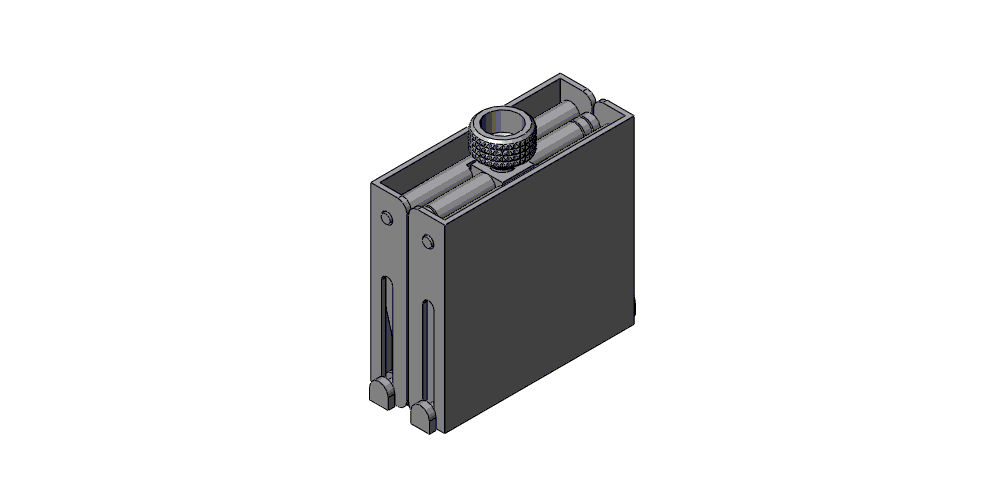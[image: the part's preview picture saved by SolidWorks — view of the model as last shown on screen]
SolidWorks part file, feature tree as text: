
SOLIDWORKS PART (.sldprt)
format: sldprt  version: not decoded by parser v0  size: 1,744,896 bytes
history: native  units: mm
features: sketch x38, extrude x17, mirror x9, cut_extrude x8, plane x5, revolve x4, boolean_combine x4, chamfer x3, pattern_linear x2, helix x2, sweep x2, cut_revolve x2, material x1, fillet x1, pattern_circular x1 (+13 scaffold rows collapsed)
feature tree (112):
  scaffold x13  (default folders/planes/origin — collapsed)
  material  "Material <not specified>"
  sketch  "Sketch1"  dims[c1.D1=80.0mm c1.D2=14.0mm c2.D1=80.0mm c2.D5=2.0mm c2.D6=1.0mm c2.D7=5.0mm]
  sketch  "Sketch2"  dims[c1.D2=2.5mm c1.D5=4.0mm c1.D6=5.0mm c1.D1=35.0mm c1.D3=35.0mm c1.D4=10.0mm c2.D1=65.0mm c2.D3=40.0mm c2.D5=60.0mm c3.D5=20.0deg c4.D5=60.0mm c5.D5=20.0deg c6.D5=60.0mm c7.D5=~8.063246deg c8.D5=80.0mm c9.D5=8.5deg c10.D5=5.25mm]
  cut_extrude  "Cut-Extrude1"  Depth=10mm
  fillet  "Fillet1"  Radius=4mm
  sketch  "Sketch3"  dims[c1.D1=3.5mm c1.D4=5.0mm c1.D2=60.0mm c2.D2=8.0deg c2.D3=~65.638792mm c2.D1=8.25mm c2.D4=1.0mm]
  extrude  "Boss-Extrude1"  Depth=3mm
  sketch  "Sketch4"  dims[c1.D1=60.0mm c2.D1=10.0deg c3.D1=~9.135154mm]
  extrude  "Boss-Extrude3"  Depth=3mm
  pattern_linear  "LPattern1"  Count1=2 Count2=1 Spacing1=9.135154mm Spacing2=10mm
  sketch  "Sketch5"
  plane  "Plane1"
  plane  "Plane2"
  plane  "Plane3"
  mirror  "Mirror1"
  mirror  "Mirror2"
  sketch  "Sketch9"
  extrude  "Boss-Extrude5"  Depth=0.65mm
  sketch  "Sketch10"  dims[D1=0.5mm]
  extrude  "Boss-Extrude6"  Depth=0.65mm
  sketch  "Sketch12"
  cut_extrude  "Cut-Extrude2"  Depth=0.2mm
  sketch  "Sketch13"  dims[D1=5.0mm]
  extrude  "Boss-Extrude8"  Depth=0.65mm
  sketch  "Sketch14"
  extrude  "Boss-Extrude9"  [1 undecoded]
  sketch  "Sketch30"
  cut_extrude  "Cut-Extrude8"  Depth=3mm
  sketch  "Sketch31"
  extrude  "Boss-Extrude18"  Depth=4.15mm
  mirror  "Mirror20"
  sketch  "Sketch23"  dims[c1.D1=1.0mm c1.D2=1.0mm c1.D3=~4.986778mm c2.D3=82.0deg c3.D3=~9.135154mm c4.D3=82.0deg c5.D3=5.125mm c6.D3=82.0deg c6.D4=~4.580357mm c7.D4=82.0deg]
  extrude  "Boss-Extrude12"  Depth=9mm
  pattern_linear  "LPattern2"  Count1=2 Count2=2 Spacing1=34.85mm Spacing2=34.85mm
  sketch  "Sketch26"
  extrude  "Boss-Extrude15"  [1 undecoded]
  sketch  "Sketch28"  dims[c1.D1=~9.135154mm c2.D1=172.0deg c3.D1=~65.638792mm c4.D1=172.0deg c5.D1=8.25mm c6.D1=82.0deg c6.D2=8.25mm c7.D2=82.0deg c8.D2=~9.135154mm c9.D2=82.0deg]
  extrude  "Boss-Extrude16"  Depth=3mm
  mirror  "Mirror14"
  sketch  "Sketch33"  dims[D1=9.0mm]
  cut_extrude  "Cut-Extrude9"  [1 undecoded]
  sketch  "Sketch35"  dims[D1=14.0mm]
  extrude  "Boss-Extrude19"  Depth=9.2mm
  sketch  "Sketch36"  dims[D1=10.0mm]
  extrude  "Boss-Extrude20"  Depth=10mm
  sketch  "Sketch65"  dims[D1=0.8mm]
  cut_extrude  "Cut-Extrude16"  Depth=2mm
  sketch  "Sketch37"  dims[c1.D1=1.0mm c1.D2=~6.385154mm c2.D1=~6.385154mm c2.D2=1.0mm c3.D1=~6.385154mm]
  cut_extrude  "Cut-Extrude10"  [1 undecoded]
  sketch  "Sketch40"  dims[c1.D1=0.8mm c1.D2=~5.985529mm c2.D2=50.0deg c2.D3=10.0mm c2.D4=0.4mm c2.D5=3.0mm c2.D6=3.0mm]
  revolve  "Revolve1"  Angle=360deg
  chamfer  "Chamfer3"  Distance=1mm Angle=45deg
  sketch  "Sketch44"
  helix  "Helix/Spiral2"  Pitch=11.25mm
  sketch  "Sketch45"  dims[D1=2.0mm D2=1.25mm]
  sweep  "Cut-Sweep1"
  plane  "Plane4"  Offset=2mm
  sketch  "Sketch47"  dims[D1=0.0mm]
  helix  "Helix/Spiral3"  Pitch=49.5mm
  sketch  "Sketch46"  dims[D1=1.25mm D2=2.0mm D3=~2.000016mm]
  sweep  "Sweep3"
  sketch  "Sketch49"
  cut_extrude  "Cut-Extrude11"  Depth=8mm
  sketch  "Sketch52"  dims[D1=0.0mm]
  extrude  "Boss-Extrude23"  Depth=10mm
  sketch  "Sketch59"  dims[c1.D1=2.0mm c1.D2=3.5mm c1.D3=3.5mm c2.D3=8.0deg]
  extrude  "Boss-Extrude24"  Depth=3.5mm
  chamfer  "Chamfer4"  Distance=3.5mm Angle=45deg
  mirror  "Mirror21"
  sketch  "Sketch60"  dims[c1.D1=8.25mm c1.D2=~10.470798mm c2.D1=0.5mm c2.D2=4.0mm]
  extrude  "Boss-Extrude25"  Depth=2mm
  mirror  "Mirror22"
  chamfer  "Chamfer5"  Distance=2mm Angle=60deg
  sketch  "Sketch62"  dims[D1=0.5mm]
  revolve  "Revolve2"  Angle=360deg
  sketch  "Sketch63"  dims[D1=2.1mm]
  cut_extrude  "Cut-Extrude15"  [1 undecoded]
  pattern_circular  "CirPattern1"  Count=32 Angle=11.25deg
  sketch  "Sketch69"
  plane  "Plane5"
  sketch  "Sketch71"  dims[c1.D1=7.5mm c1.D2=~2.179387mm c2.D2=45.0deg c2.D1=0.75mm c3.D2=2.5mm]
  cut_revolve  "Cut-Revolve1"  Angle=360deg
  sketch  "Sketch74"
  cut_revolve  "Cut-Revolve2"  Angle=360deg
  mirror  "Mirror23"
  sketch  "Sketch72"  dims[c1.D1=~1.228622mm c2.D1=45.0deg c3.D1=1.125mm c4.D1=45.0deg]
  revolve  "Revolve3"  Angle=360deg
  sketch  "Sketch75"
  revolve  "Revolve4"  Angle=360deg
  mirror  "Mirror24"
  sketch  "Sketch76"  dims[D1=3.0mm]
  extrude  "Boss-Extrude26"  Depth=3mm
  sketch  "Sketch77"
  extrude  "Boss-Extrude27"  Depth=3mm
  mirror  "Mirror31"
  boolean_combine  "Combine1"
  boolean_combine  "Combine2"
  boolean_combine  "Combine3"
  boolean_combine  "Combine4"
decode coverage: 60 of 93 modeling features carry decoded parameters
note: ~ marks probable driven/reference dimensions
note: 5 parameter values undecoded
summary: no parameter record found for 5 features
note: suppression state not decoded; provenance and decode notes live in map.json
